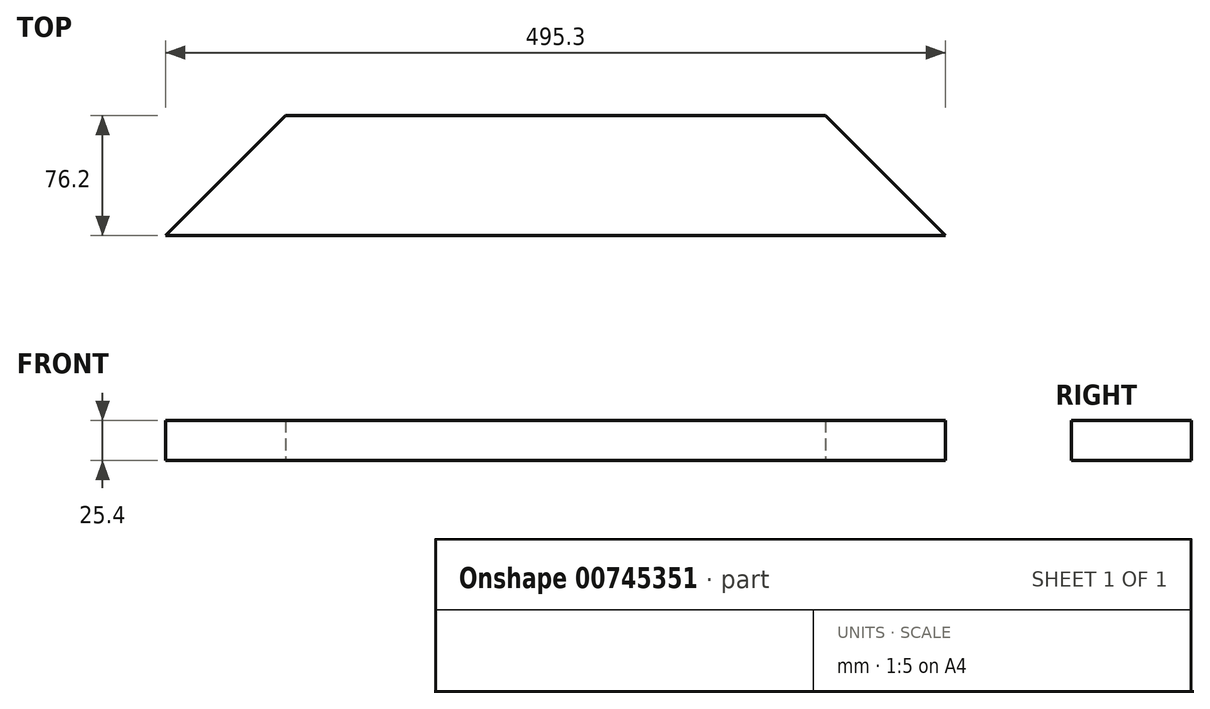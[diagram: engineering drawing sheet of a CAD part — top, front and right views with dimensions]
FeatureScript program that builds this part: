
annotation { "Feature Type Name" : "Feature", "Feature Type Description" : "" }
export const myFeature = defineFeature(function(context is Context, id is Id, definition is map)
    precondition{}
    {
        {
            var Q0;
            Q0=qCreatedBy(makeId("Top.planeOp"),FACE);
            var sketch = newSketch(context, id + "F0", { "sketchPlane" : qUnion([Q0])});
            skLineSegment(sketch, "E0.bottom", {"start": v(0, 0) * mm, "end": v(495.3, 0) * mm});
            skLineSegment(sketch, "E0.top", {"start": v(76.2, 76.2) * mm, "end": v(419.1, 76.2) * mm});
            skLineSegment(sketch, "E1", {"start": v(0, 0) * mm, "end": v(76.2, 76.2) * mm});
            skLineSegment(sketch, "E2", {"start": v(495.3, 0) * mm, "end": v(419.1, 76.2) * mm});
            skSolve(sketch);
        }
        {
            var Q0;
            Q0=makeQuery(id+"F0.imprint","IMPRINT",FACE,{"disambiguationData":[TD([[makeQuery(id+"F0.imprint","IMPRINT",EDGE,{"derivedFrom":sQuery(id+"F0.wireOp",EDGE,"E0.bottom")}),1.0]])]});
            extrude(context, id + "F1", {"entities" : qUnion([Q0]), "depth" : 25.4 * mm, "offsetDistance" : 25.4 * mm});
        }
    });
